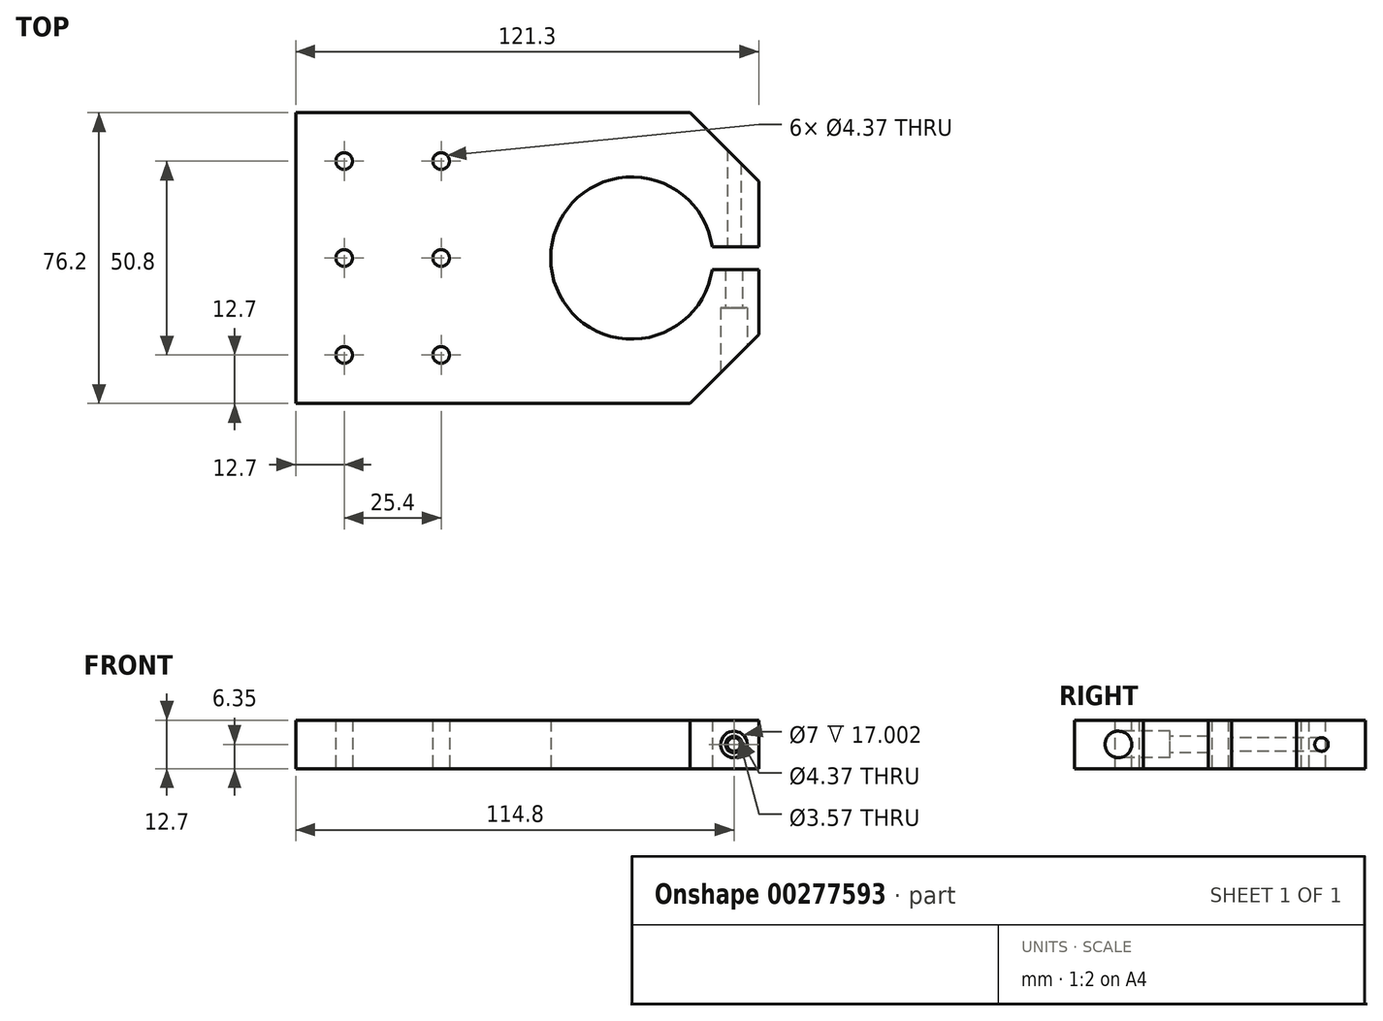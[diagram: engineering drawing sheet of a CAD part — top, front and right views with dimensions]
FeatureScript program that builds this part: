
annotation { "Feature Type Name" : "Feature", "Feature Type Description" : "" }
export const myFeature = defineFeature(function(context is Context, id is Id, definition is map)
    precondition{}
    {
        {
            var Q0;
            Q0=qCreatedBy(makeId("Top.planeOp"),FACE);
            var sketch = newSketch(context, id + "F0", { "sketchPlane" : qUnion([Q0])});
            skCircle(sketch, "E0", {"center": v(0, 0) * mm, "radius": 21.25 * mm});
            skLineSegment(sketch, "E1.bottom", {"start": v(-88.05, 38.1) * mm, "end": v(33.25, 38.1) * mm});
            skLineSegment(sketch, "E1.top", {"start": v(-88.05, -38.1) * mm, "end": v(33.25, -38.1) * mm});
            skLineSegment(sketch, "E1.left", {"start": v(-88.05, 38.1) * mm, "end": v(-88.05, -38.1) * mm});
            skLineSegment(sketch, "E1.right", {"start": v(33.25, 38.1) * mm, "end": v(33.25, -38.1) * mm});
            skLineSegment(sketch, "E2.bottom", {"start": v(-88.05, 89.65) * mm, "end": v(-37.25, 89.65) * mm, "construction": true});
            skLineSegment(sketch, "E2.top", {"start": v(-88.05, -62.75) * mm, "end": v(-37.25, -62.75) * mm, "construction": true});
            skLineSegment(sketch, "E2.left", {"start": v(-88.05, 89.65) * mm, "end": v(-88.05, -62.75) * mm, "construction": true});
            skLineSegment(sketch, "E2.right", {"start": v(-37.25, 89.65) * mm, "end": v(-37.25, -62.75) * mm, "construction": true});
            skLineSegment(sketch, "E3.bottom", {"start": v(0, -3) * mm, "end": v(33.25, -3) * mm});
            skLineSegment(sketch, "E3.top", {"start": v(0, 3) * mm, "end": v(33.25, 3) * mm});
            skLineSegment(sketch, "E3.left", {"start": v(0, 3) * mm, "end": v(0, -3) * mm});
            skLineSegment(sketch, "E3.right", {"start": v(33.25, 3) * mm, "end": v(33.25, -3) * mm});
            skLineSegment(sketch, "E4", {"start": v(15.25, 38.1) * mm, "end": v(33.25, 20.1) * mm});
            skLineSegment(sketch, "E5", {"start": v(15.25, -38.1) * mm, "end": v(33.25, -20.1) * mm});
            skLineSegment(sketch, "E6.bottom", {"start": v(-75.35, 25.4) * mm, "end": v(-49.95, 25.4) * mm, "construction": true});
            skLineSegment(sketch, "E6.top", {"start": v(-75.35, -25.4) * mm, "end": v(-49.95, -25.4) * mm, "construction": true});
            skLineSegment(sketch, "E6.left", {"start": v(-75.35, 25.4) * mm, "end": v(-75.35, -25.4) * mm, "construction": true});
            skLineSegment(sketch, "E6.right", {"start": v(-49.95, 25.4) * mm, "end": v(-49.95, -25.4) * mm, "construction": true});
            skCircle(sketch, "E7", {"center": v(-75.35, 25.4) * mm, "radius": 2.18 * mm});
            skCircle(sketch, "E8", {"center": v(-75.35, 0) * mm, "radius": 2.18 * mm});
            skCircle(sketch, "E9", {"center": v(-75.35, -25.4) * mm, "radius": 2.18 * mm});
            skCircle(sketch, "E10", {"center": v(-49.95, -25.4) * mm, "radius": 2.18 * mm});
            skCircle(sketch, "E11", {"center": v(-49.95, 0) * mm, "radius": 2.18 * mm});
            skCircle(sketch, "E12", {"center": v(-49.95, 25.4) * mm, "radius": 2.18 * mm});
            skSolve(sketch);
        }
        {
            var Q0;
            {var subQ0=sQuery(id+"F0.wireOp",EDGE,"E1.left");Q0=makeQuery(id+"F0.imprint","IMPRINT",FACE,{"disambiguationData":[TD([[makeQuery(id+"F0.imprint","IMPRINT",EDGE,{"derivedFrom":subQ0}),1.0]])]});}
            extrude(context, id + "F1", {"entities" : qUnion([Q0]), "endBound" : BoundingType.SYMMETRIC, "depth" : 12.7 * mm, "offsetDistance" : 25 * mm});
        }
        {
            var Q0;
            Q0=makeQuery(id+"F1.opExtrude","SWEPT_FACE",FACE,{"disambiguationData":[OSD([sQuery(id+"F0.wireOp",EDGE,"E1.top")])]});
            var sketch = newSketch(context, id + "F2", { "sketchPlane" : qUnion([Q0])});
            skCircle(sketch, "E13", {"center": v(26.75, 0) * mm, "radius": 3.5 * mm});
            skCircle(sketch, "E14", {"center": v(26.75, 0) * mm, "radius": 2.18 * mm});
            skCircle(sketch, "E15", {"center": v(26.75, 0) * mm, "radius": 1.79 * mm});
            skSolve(sketch);
        }
        {
            var Q0;
            Q0=makeQuery(id+"F2.imprint","IMPRINT",FACE,{"disambiguationData":[TD([[makeQuery(id+"F2.imprint","IMPRINT",EDGE,{"derivedFrom":sQuery(id+"F2.wireOp",EDGE,"E13")}),1.0]])]});
            var Q1;
            Q1=makeQuery(id+"F1.opExtrude","SWEPT_FACE",FACE,{"disambiguationData":[OSD([sQuery(id+"F0.wireOp",EDGE,"E3.bottom")])]});
            extrude(context, id + "F3", {"entities" : qUnion([Q0]), "operationType" : NewBodyOperationType.REMOVE, "oppositeDirection" : true, "depth" : 25 * mm, "endBoundEntityFace" : qUnion([Q1]), "offsetDistance" : 25 * mm});
        }
        {
            var Q0;
            Q0=makeQuery(id+"F2.imprint","IMPRINT",FACE,{"disambiguationData":[TD([[makeQuery(id+"F2.imprint","IMPRINT",EDGE,{"derivedFrom":sQuery(id+"F2.wireOp",EDGE,"E14")}),1.0]])]});
            var Q1;
            Q1=makeQuery(id+"F2.imprint","IMPRINT",FACE,{"disambiguationData":[TD([[makeQuery(id+"F2.imprint","IMPRINT",EDGE,{"derivedFrom":sQuery(id+"F2.wireOp",EDGE,"E15")}),1.0]])]});
            var Q2;
            Q2=makeQuery(id+"F1.opExtrude","SWEPT_FACE",FACE,{"disambiguationData":[OSD([sQuery(id+"F0.wireOp",EDGE,"E3.bottom")])]});
            extrude(context, id + "F4", {"entities" : qUnion([Q0, Q1]), "operationType" : NewBodyOperationType.REMOVE, "endBound" : BoundingType.UP_TO_SURFACE, "oppositeDirection" : true, "depth" : 25 * mm, "endBoundEntityFace" : qUnion([Q2]), "offsetDistance" : 25 * mm});
        }
        {
            var Q0;
            Q0=makeQuery(id+"F2.imprint","IMPRINT",FACE,{"disambiguationData":[TD([[makeQuery(id+"F2.imprint","IMPRINT",EDGE,{"derivedFrom":sQuery(id+"F2.wireOp",EDGE,"E15")}),1.0]])]});
            var Q1;
            Q1=makeQuery(id+"F1.opExtrude","SWEPT_FACE",FACE,{"disambiguationData":[OSD([sQuery(id+"F0.wireOp",EDGE,"E1.bottom")])]});
            extrude(context, id + "F5", {"entities" : qUnion([Q0]), "operationType" : NewBodyOperationType.REMOVE, "endBound" : BoundingType.UP_TO_SURFACE, "oppositeDirection" : true, "depth" : 71.1 * mm, "endBoundEntityFace" : qUnion([Q1]), "offsetDistance" : 25 * mm});
        }
    });
